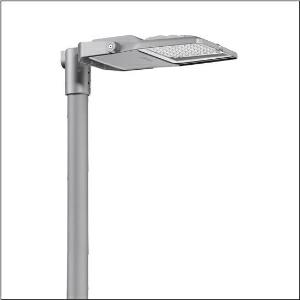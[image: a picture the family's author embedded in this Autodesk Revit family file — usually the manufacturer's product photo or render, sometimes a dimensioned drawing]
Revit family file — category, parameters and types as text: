
# Revit family: floodlight_fl_21_iq_mini___pl52_5xa7772c4d3a_40ba
name_source: partatom
category: Lighting Fixtures
units: mm (PartAtom-declared; Revit-internal decimal feet)

## family parameters
Cut with Voids When Loaded = No
Host = Face
Light Source = No
Part Type = Normal
Room Calculation Point = No
Round Connector Dimension = Use Diameter
Shared = No

## types (1)
- --- (1 x LED, 12720 lm, 87.2 W, 4000K)
    Apparent Load = 87 VA
    CIE Flux Codes = 26 60 98 100 100
    Color Rendering = 70
    Color Temperature = 4000K
    Default Elevation = 1800 mm
    Description = Floodlight FL 21 iQ mini, floodlight, primary light control with lens, of PMMA, primary optical cover: protective disc, of toughened safety glass, transparent, light distribution: PL52, light emission: direct distribution, installation type: surface-mounted, LED, High Power LED, rated luminous flux: 12.720lm, luminous efficacy: 146lm/W, light colour: 740, colour temperature: 4000K, control: Auto-Match, Temp-Guard, Night-Set, Smart-Wire, Desk-Remote (wireless, voltage-free reading and setting of iQ features in the workshop via application-optimized NFC function/RFID function), optimised constant luminous flux control (CLO 2.0), Light-Fading, Lumen-Switch, with terminal, 6-pole, mains connection: 220..240V, AC, 50/60Hz, start of lifetime: 87W, end of service life: 92W, reduction: 40W, luminaire housing, of diecast aluminium, powder-coated, Siteco® metallic grey (DB 702S), corrosivity category C5 mid according to DIN EN ISO 12944, sealing non-destructively replaceable, please order mast flange separately, mast bracket, of steel, galvanised, powder-coated, protection rating (complete): IP66, insulation class (complete): insulation class II (safety insulation), certification: CE, ENEC, VDE, protection symbol: D, impact resistance: IK08, permissible operating ambient temperature: -40..+40°C, permissible operating ambient temperature for outdoor applications: -40..+50°C, standard: DIN EN 12944, LABS conformity tested according to VDMA 24364:2018-05, packaging unit: 1 piece

Light Distribution: PL52
    Height = 70 mm
    Lamp = 1 x LED
    Lamp Light Flux = 12720 lm
    Lamp Power = 87.2 W
    Lamp count = 1
    Length = 485 mm
    Luminous efficacy = 146 lm/W
    Manufacturer = Siteco
    ModVariant = No
    Model = 5XA7772C4D3A
    Number of Poles = 1
    OnlyDefault = Yes
    Power Factor = 1
    Product Name = Floodlight FL 21 iQ mini | PL52
    Product group = floodlight | pylon annexe
    ProductGroupID = 6200
    Protection Class = Protection class II
    Protection Degree = IP 66
    RLX_Detail_Level = 1
    RLX_Emergency_Light_Flux = 0 lm
    RLX_Emergency_Type = 0
    RLX_Emergency_Type_DB = No
    RlxData = <blob elided: 101605 chars, md5=d4133a4c>
    Socket = socket
    Standby Power = 0 W
    System Light Flux = 12720 lm
    System Power = 87 W
    Type Comments = factory setting: luminous flux: 100 % | dim-lin: 254 | 456 mA
    Type Image = l_1007125.jpg
    URL = http://relux.com
    VarID = @adj_096459
    Voltage = 0 V
    Weight = 0.00 kg
    Width = 337 mm

## geometry (parser evidence)
native form markers: Blend x4, Sweep x12
no freeform markers — native parametric forms only
